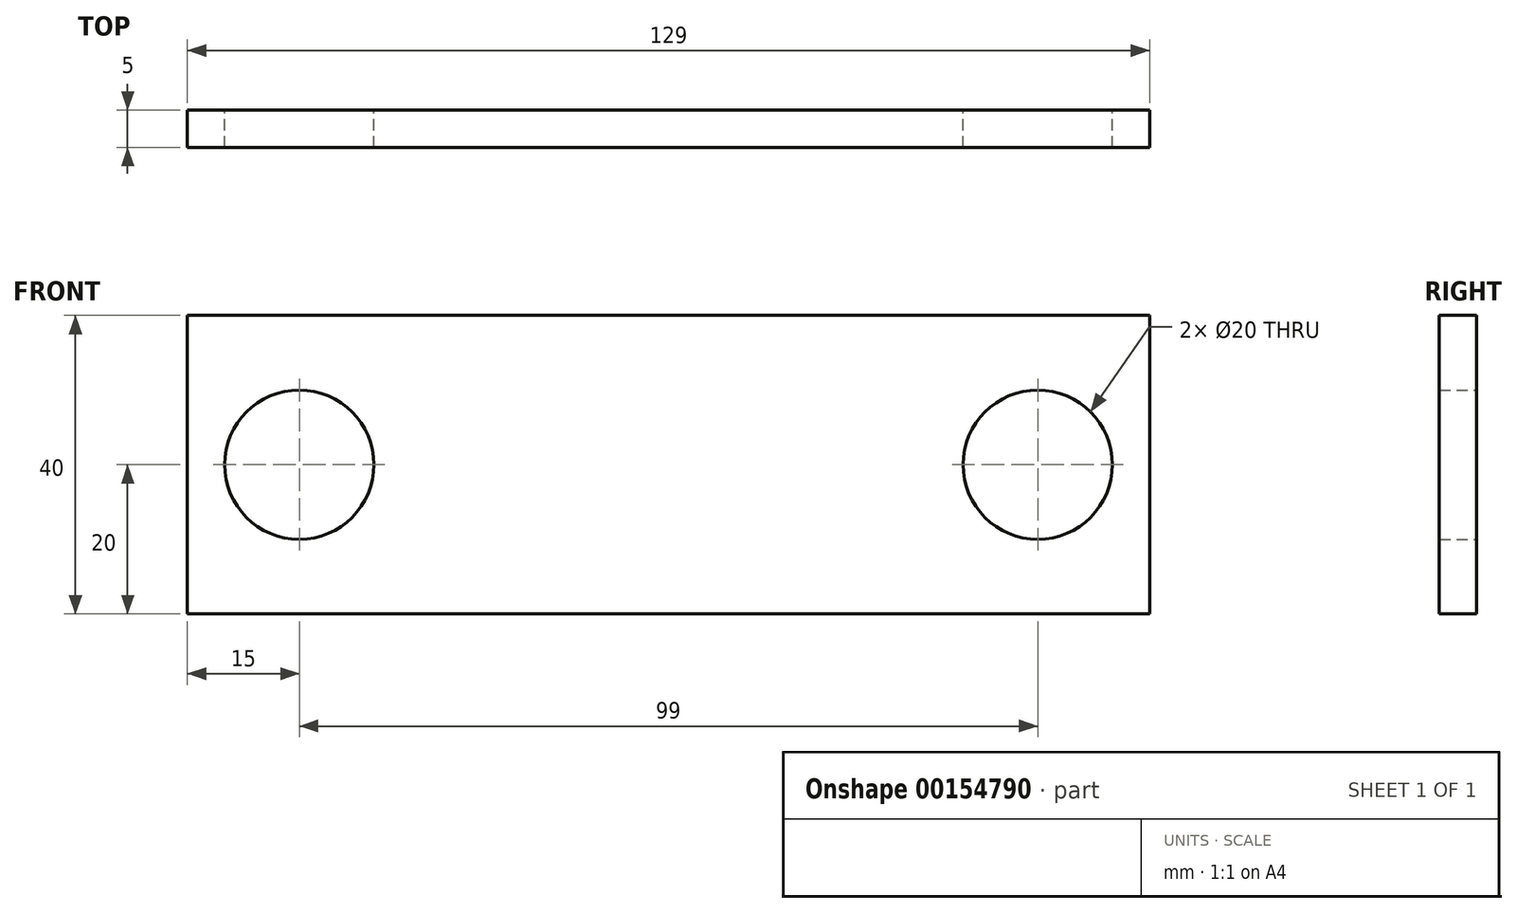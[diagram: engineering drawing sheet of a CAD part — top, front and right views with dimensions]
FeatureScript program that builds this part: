
annotation { "Feature Type Name" : "Feature", "Feature Type Description" : "" }
export const myFeature = defineFeature(function(context is Context, id is Id, definition is map)
    precondition{}
    {
        {
            var Q0;
            Q0=qCreatedBy(makeId("Front.planeOp"),FACE);
            var sketch = newSketch(context, id + "F0", { "sketchPlane" : qUnion([Q0])});
            skLineSegment(sketch, "E0.bottom", {"start": v(0, 0) * mm, "end": v(129, 0) * mm});
            skLineSegment(sketch, "E0.top", {"start": v(0, 40) * mm, "end": v(129, 40) * mm});
            skLineSegment(sketch, "E0.left", {"start": v(0, 0) * mm, "end": v(0, 40) * mm});
            skLineSegment(sketch, "E0.right", {"start": v(129, 0) * mm, "end": v(129, 40) * mm});
            skCircle(sketch, "E1", {"center": v(15, 20) * mm, "radius": 10 * mm});
            skPoint(sketch, "E1.centerSnap0", {"position": v(0, 20) * mm});
            skCircle(sketch, "E2", {"center": v(114, 20) * mm, "radius": 10 * mm});
            skPoint(sketch, "E2.centerSnap0", {"position": v(129, 20) * mm});
            skSolve(sketch);
        }
        {
            var Q0;
            Q0 = qSketchRegion(id + "F0", true);
            extrude(context, id + "F1", {"entities" : qUnion([Q0]), "depth" : 5 * mm});
        }
    });
